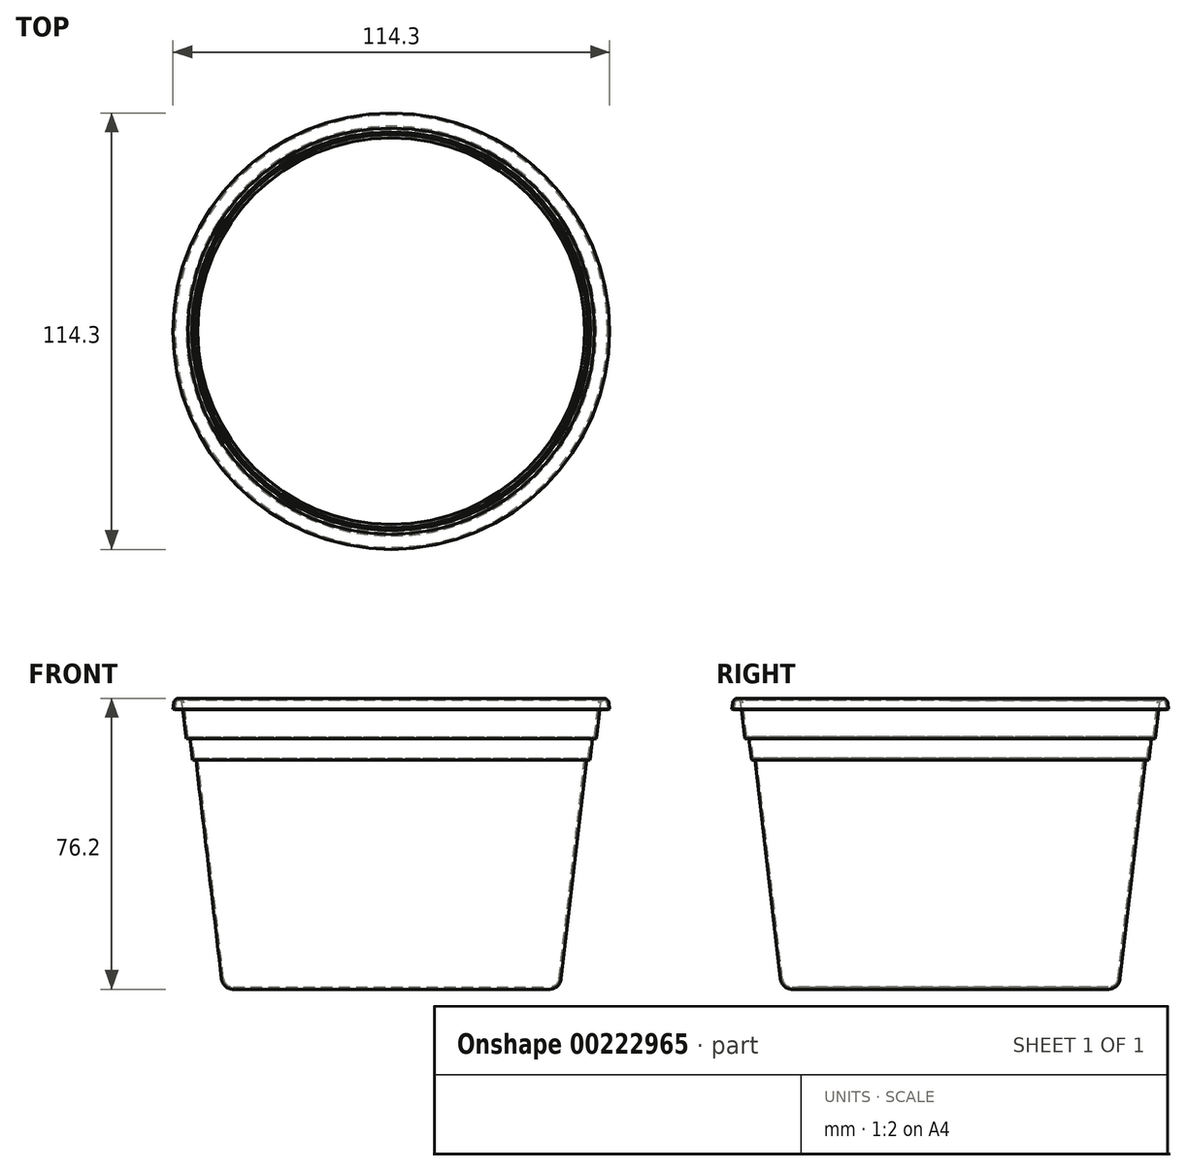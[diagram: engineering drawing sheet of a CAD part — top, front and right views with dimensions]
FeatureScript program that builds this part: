
annotation { "Feature Type Name" : "Feature", "Feature Type Description" : "" }
export const myFeature = defineFeature(function(context is Context, id is Id, definition is map)
    precondition{}
    {
        {
            var Q0;
            Q0=qCreatedBy(makeId("Front.planeOp"),FACE);
            var sketch = newSketch(context, id + "F0", { "sketchPlane" : qUnion([Q0])});
            skLineSegment(sketch, "E0", {"start": v(0, 0) * mm, "end": v(0, 55.94) * mm, "construction": true});
            skLineSegment(sketch, "E1", {"start": v(0, 0) * mm, "end": v(-41.4, 0) * mm});
            skLineSegment(sketch, "E2", {"start": v(-44.45, 2.72) * mm, "end": v(-51.13, 60) * mm});
            skLineSegment(sketch, "E3", {"start": v(-51.13, 60) * mm, "end": v(-52.02, 60) * mm});
            skLineSegment(sketch, "E4", {"start": v(-52.02, 60) * mm, "end": v(-52.67, 65.6) * mm});
            skLineSegment(sketch, "E5", {"start": v(-52.67, 65.6) * mm, "end": v(-53.7, 65.6) * mm});
            skLineSegment(sketch, "E6", {"start": v(-53.7, 65.6) * mm, "end": v(-54.78, 74.93) * mm});
            skLineSegment(sketch, "E7", {"start": v(-56.62, 73.28) * mm, "end": v(-56.43, 74.93) * mm});
            skArc(sketch, "E8", {"start": v(-54.78, 74.93) * mm, "mid": v(-55.6, 75.67) * mm, "end": v(-56.43, 74.93) * mm});
            skArc(sketch, "E9.filletArc", {"start": v(-44.45, 2.72) * mm, "mid": v(-43.44, 0.78) * mm, "end": v(-41.4, 0) * mm});
            skLineSegment(sketch, "E10.0", {"start": v(-57.15, 73.34) * mm, "end": v(-56.96, 75) * mm});
            skArc(sketch, "E10.1", {"start": v(-54.25, 75) * mm, "mid": v(-55.6, 76.2) * mm, "end": v(-56.96, 75) * mm});
            skLineSegment(sketch, "E10.2", {"start": v(-53.22, 66.14) * mm, "end": v(-54.25, 75) * mm});
            skLineSegment(sketch, "E10.3", {"start": v(-52.2, 66.14) * mm, "end": v(-53.22, 66.14) * mm});
            skLineSegment(sketch, "E10.4", {"start": v(-51.55, 60.53) * mm, "end": v(-52.2, 66.14) * mm});
            skLineSegment(sketch, "E10.5", {"start": v(0, 0.53) * mm, "end": v(-41.4, 0.53) * mm});
            skArc(sketch, "E10.6", {"start": v(-43.92, 2.78) * mm, "mid": v(-43.09, 1.18) * mm, "end": v(-41.4, 0.53) * mm});
            skLineSegment(sketch, "E10.7", {"start": v(-43.92, 2.78) * mm, "end": v(-50.66, 60.53) * mm});
            skLineSegment(sketch, "E10.8", {"start": v(-50.66, 60.53) * mm, "end": v(-51.55, 60.53) * mm});
            skLineSegment(sketch, "E11", {"start": v(-57.15, 73.34) * mm, "end": v(-56.62, 73.28) * mm});
            skLineSegment(sketch, "E12", {"start": v(-55.6, 76.2) * mm, "end": v(-58.47, 76.2) * mm, "construction": true});
            skPoint(sketch, "E12.startSnap0", {"position": v(-55.6, 76.2) * mm});
            skLineSegment(sketch, "E13", {"start": v(0, 0.53) * mm, "end": v(0, 0) * mm});
            skSolve(sketch);
        }
        {
            var Q0;
            Q0=makeQuery(id+"F0.imprint","IMPRINT",FACE,{"disambiguationData":[TD([[makeQuery(id+"F0.imprint","IMPRINT",EDGE,{"derivedFrom":sQuery(id+"F0.wireOp",EDGE,"E1")}),-1.0]])]});
            var Q1;
            Q1=sQuery(id+"F0.wireOp",EDGE,"E0");
            revolve(context, id + "F1", {"entities" : qUnion([Q0]), "axis" : qUnion([Q1]), "revolveType" : RevolveType.FULL});
        }
    });
